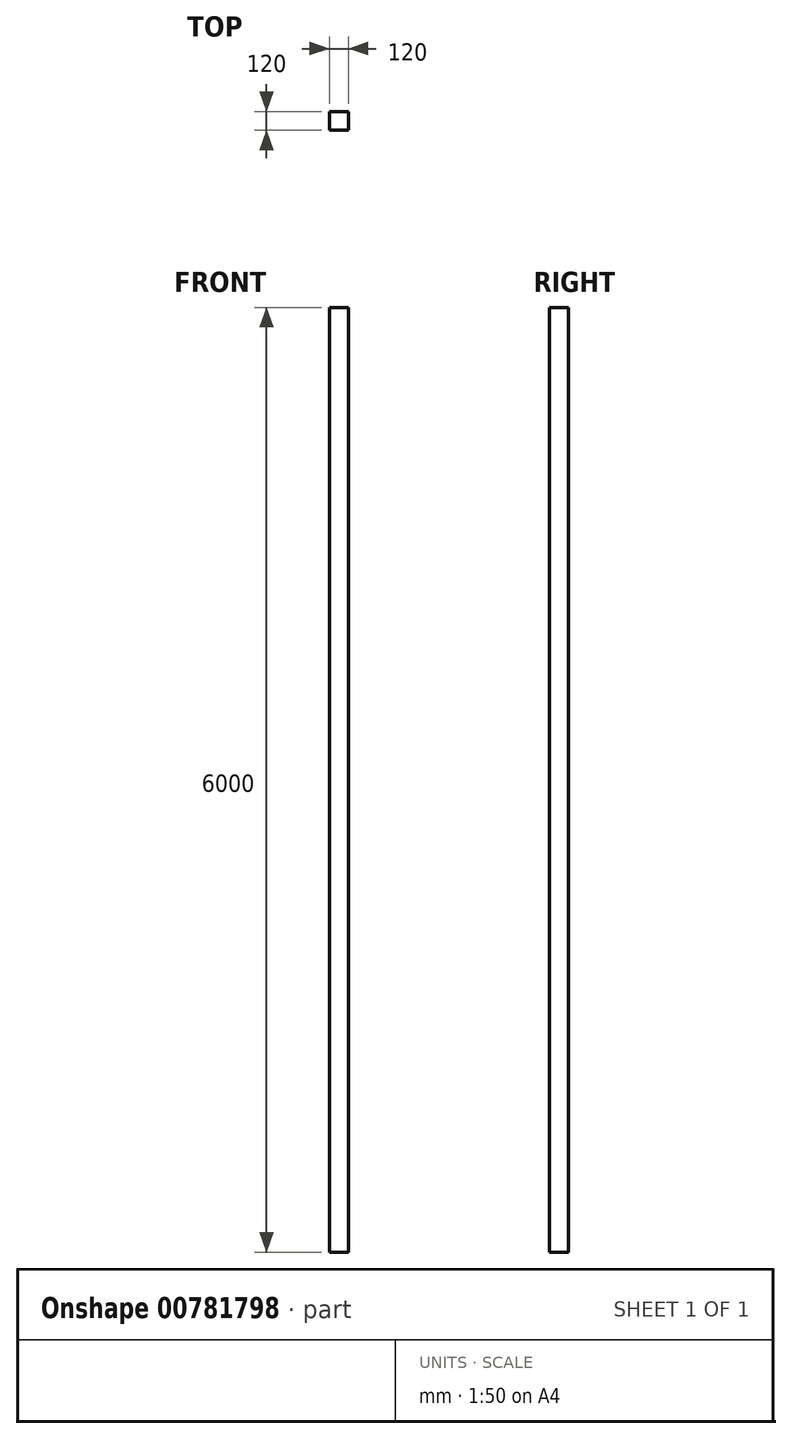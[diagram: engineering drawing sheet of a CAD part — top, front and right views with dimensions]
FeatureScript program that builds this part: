
annotation { "Feature Type Name" : "Feature", "Feature Type Description" : "" }
export const myFeature = defineFeature(function(context is Context, id is Id, definition is map)
    precondition{}
    {
        {
            var Q0;
            Q0=qCreatedBy(makeId("Top.planeOp"),FACE);
            var sketch = newSketch(context, id + "F0", { "sketchPlane" : qUnion([Q0])});
            skLineSegment(sketch, "E0.bottom", {"start": v(-120, -120) * mm, "end": v(0, -120) * mm});
            skLineSegment(sketch, "E0.top", {"start": v(-120, 0) * mm, "end": v(0, 0) * mm});
            skLineSegment(sketch, "E0.left", {"start": v(-120, -120) * mm, "end": v(-120, 0) * mm});
            skLineSegment(sketch, "E0.right", {"start": v(0, -120) * mm, "end": v(0, 0) * mm});
            skSolve(sketch);
        }
        {
            var Q0;
            Q0=makeQuery(id+"F0.imprint","IMPRINT",FACE,{"disambiguationData":[TD([[makeQuery(id+"F0.imprint","IMPRINT",EDGE,{"derivedFrom":sQuery(id+"F0.wireOp",EDGE,"E0.bottom")}),1.0]])]});
            extrude(context, id + "F1", {"entities" : qUnion([Q0]), "depth" : 6000 * mm, "offsetDistance" : 25 * mm});
        }
    });
